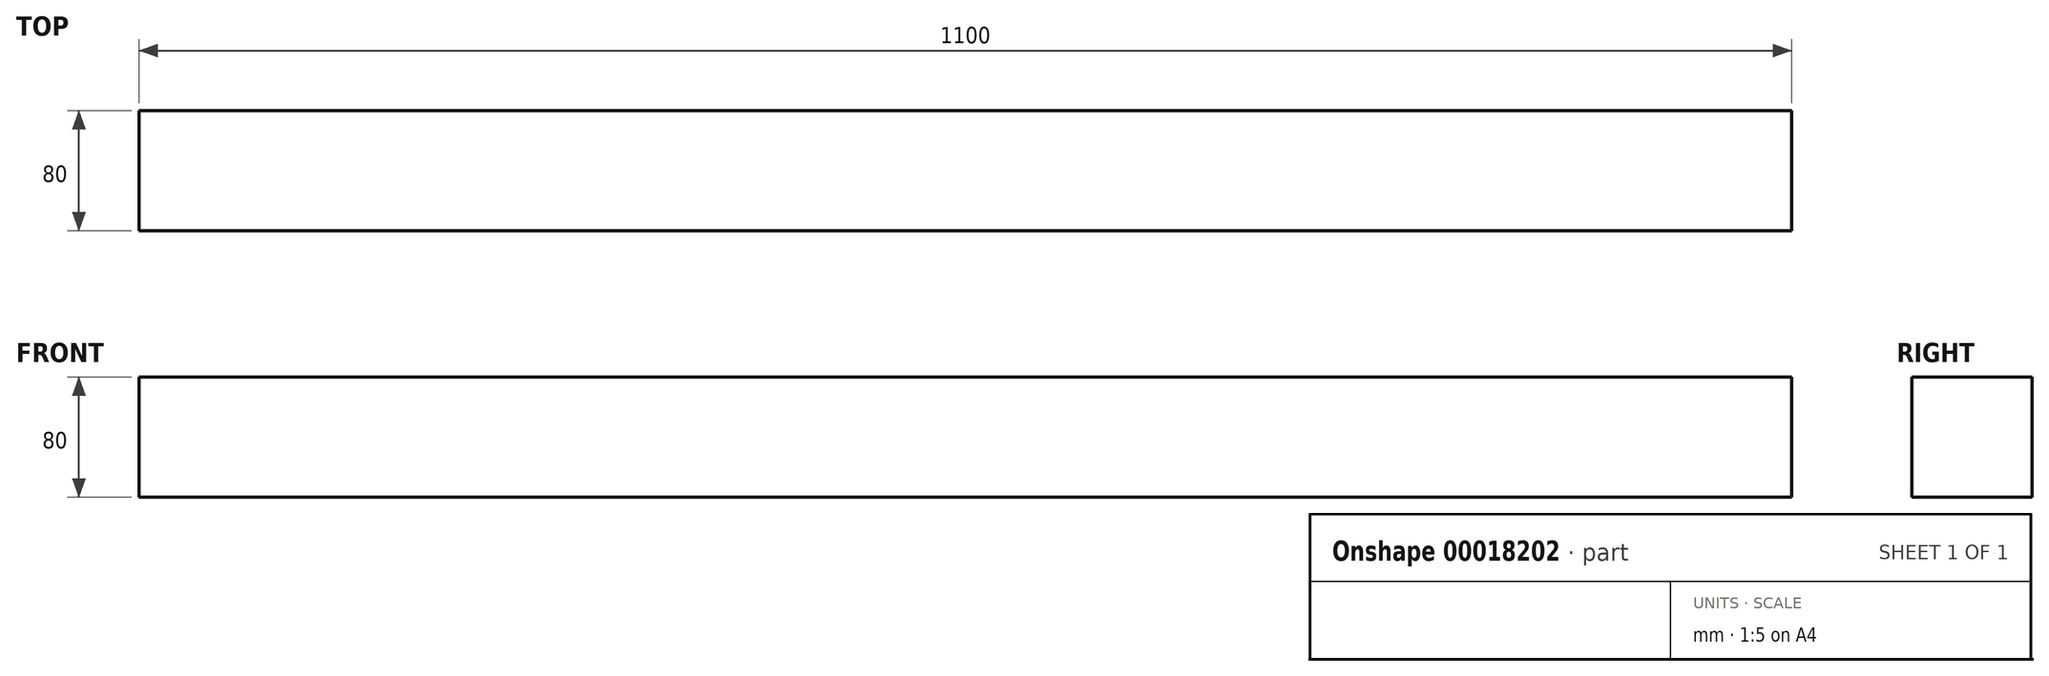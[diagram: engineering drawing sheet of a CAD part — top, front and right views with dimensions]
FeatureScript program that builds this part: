
annotation { "Feature Type Name" : "Feature", "Feature Type Description" : "" }
export const myFeature = defineFeature(function(context is Context, id is Id, definition is map)
    precondition{}
    {
        {
            var Q0;
            Q0=qCreatedBy(makeId("Top.planeOp"),FACE);
            var sketch = newSketch(context, id + "F0", { "sketchPlane" : qUnion([Q0])});
            skLineSegment(sketch, "E0.bottom", {"start": v(0, 0) * mm, "end": v(1100, 0) * mm});
            skLineSegment(sketch, "E0.top", {"start": v(0, 80) * mm, "end": v(1100, 80) * mm});
            skLineSegment(sketch, "E0.left", {"start": v(0, 0) * mm, "end": v(0, 80) * mm});
            skLineSegment(sketch, "E0.right", {"start": v(1100, 0) * mm, "end": v(1100, 80) * mm});
            skSolve(sketch);
        }
        {
            var Q0;
            Q0=makeQuery(id+"F0.imprint","IMPRINT",FACE,{"disambiguationData":[TD([[makeQuery(id+"F0.imprint","IMPRINT",EDGE,{"derivedFrom":sQuery(id+"F0.wireOp",EDGE,"E0.bottom")}),1.0]])]});
            extrude(context, id + "F1", {"entities" : qUnion([Q0]), "depth" : 80 * mm});
        }
    });
